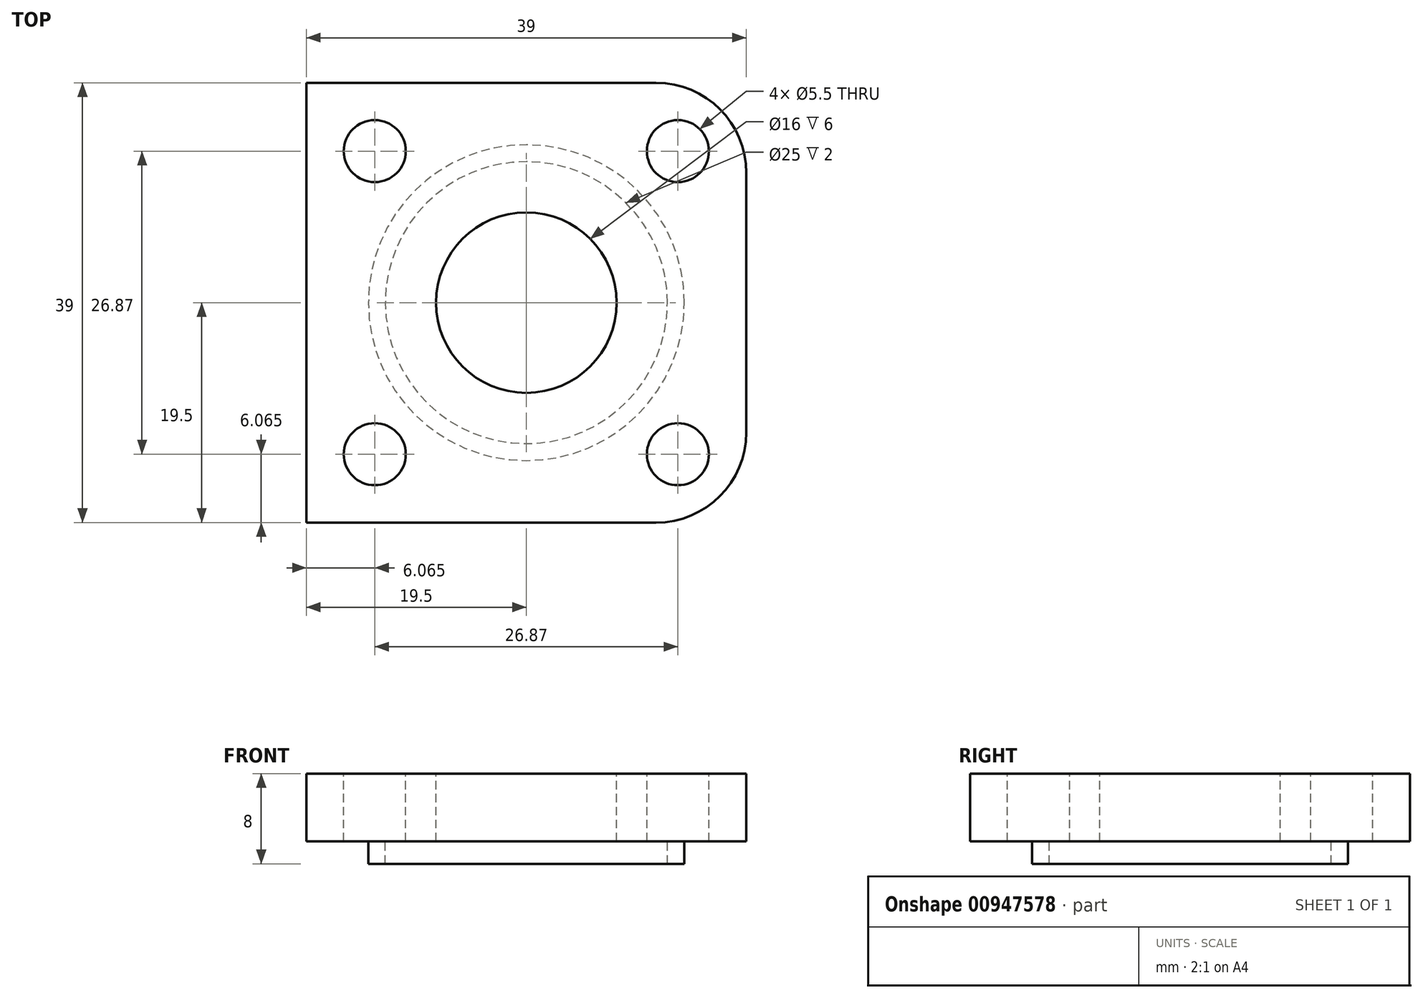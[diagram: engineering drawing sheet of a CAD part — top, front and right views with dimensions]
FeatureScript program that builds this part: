
annotation { "Feature Type Name" : "Feature", "Feature Type Description" : "" }
export const myFeature = defineFeature(function(context is Context, id is Id, definition is map)
    precondition{}
    {
        {
            var Q0;
            Q0=qCreatedBy(makeId("Top.planeOp"),FACE);
            var sketch = newSketch(context, id + "F0", { "sketchPlane" : qUnion([Q0])});
            skLineSegment(sketch, "E0", {"start": v(0, 0) * mm, "end": v(0, -19.5) * mm});
            skLineSegment(sketch, "E1", {"start": v(0, -19.5) * mm, "end": v(31, -19.5) * mm});
            skLineSegment(sketch, "E2", {"start": v(39, -11.5) * mm, "end": v(39, 11.5) * mm});
            skLineSegment(sketch, "E3", {"start": v(31, 19.5) * mm, "end": v(0, 19.5) * mm});
            skLineSegment(sketch, "E4", {"start": v(0, 19.5) * mm, "end": v(0, 0) * mm});
            skCircle(sketch, "E5", {"center": v(19.5, 0) * mm, "radius": 8 * mm});
            skPoint(sketch, "E6.visualSharp", {"position": v(39, 19.5) * mm});
            skArc(sketch, "E6.filletArc", {"start": v(39, 11.5) * mm, "mid": v(36.66, 17.16) * mm, "end": v(31, 19.5) * mm});
            skPoint(sketch, "E7.visualSharp", {"position": v(39, -19.5) * mm});
            skArc(sketch, "E7.filletArc", {"start": v(31, -19.5) * mm, "mid": v(36.66, -17.16) * mm, "end": v(39, -11.5) * mm});
            skCircle(sketch, "E8", {"center": v(32.94, 13.44) * mm, "radius": 2.75 * mm});
            skCircle(sketch, "E9", {"center": v(6.06, 13.44) * mm, "radius": 2.75 * mm});
            skCircle(sketch, "E10", {"center": v(6.06, -13.44) * mm, "radius": 2.75 * mm});
            skCircle(sketch, "E11", {"center": v(32.94, -13.44) * mm, "radius": 2.75 * mm});
            skSolve(sketch);
        }
        {
            var Q0;
            Q0=makeQuery(id+"F0.imprint","IMPRINT",FACE,{"disambiguationData":[TD([[makeQuery(id+"F0.imprint","IMPRINT",EDGE,{"derivedFrom":sQuery(id+"F0.wireOp",EDGE,"E0")}),1.0]])]});
            extrude(context, id + "F1", {"entities" : qUnion([Q0]), "oppositeDirection" : true, "depth" : 6 * mm, "offsetDistance" : 25 * mm});
        }
        {
            var Q0;
            Q0=makeQuery(id+"F1.opExtrude","CAP_FACE",FACE,{"disambiguationData":[OSD([sQuery(id+"F0.wireOp",EDGE,"E0"),sQuery(id+"F0.wireOp",EDGE,"E1"),sQuery(id+"F0.wireOp",EDGE,"E2"),sQuery(id+"F0.wireOp",EDGE,"E3"),sQuery(id+"F0.wireOp",EDGE,"E4"),sQuery(id+"F0.wireOp",EDGE,"E5"),sQuery(id+"F0.wireOp",EDGE,"E6.filletArc"),sQuery(id+"F0.wireOp",EDGE,"E7.filletArc"),sQuery(id+"F0.wireOp",EDGE,"E8"),sQuery(id+"F0.wireOp",EDGE,"E9"),sQuery(id+"F0.wireOp",EDGE,"E10"),sQuery(id+"F0.wireOp",EDGE,"E11")])],"isStart":false});
            var sketch = newSketch(context, id + "F2", { "sketchPlane" : qUnion([Q0])});
            skCircle(sketch, "E12", {"center": v(19.5, 0) * mm, "radius": 12.5 * mm});
            skCircle(sketch, "E13", {"center": v(19.5, 0) * mm, "radius": 14 * mm});
            skSolve(sketch);
        }
        {
            var Q0;
            Q0=makeQuery(id+"F2.imprint","IMPRINT",FACE,{"disambiguationData":[TD([[makeQuery(id+"F2.imprint","IMPRINT",EDGE,{"derivedFrom":sQuery(id+"F2.wireOp",EDGE,"E12")}),-1.0]])]});
            extrude(context, id + "F3", {"entities" : qUnion([Q0]), "operationType" : NewBodyOperationType.ADD, "depth" : 2 * mm, "offsetDistance" : 25 * mm});
        }
    });
